# Revit family: Electronics_Visual-Projectors_ViewSonic_The-ViewSonicR-PRO8510L-Projector
name_source: partatom
category: Electrical Equipment
revit_build: Autodesk Revit 2015 (Build: 20140606_1530(x64)
units: mm (PartAtom-declared; Revit-internal decimal feet)

## types (1)
- PRO8510L
    Assembly Code = D50
    BIMobject category = Visual - Projectors
    BIMobject category code = electronics-visual-projectors
    BIMobject main category = Electronics
    BIMobject main category code = electronics
    BOSUseNativeGeometries = 1
    Brand url = https://www.viewsonic.com
    Covering Color = Plastic - Viewsonic - White
    Description = Delivering 1024 x 768 resolution and 5200 lumens of brightness, the ViewSonic® LightStream® Pro8510L is the ideal XGA projector for professional installations, large venues, and business and education environments. With its 1.6x optical zoom, centered lens, vertical lens shift, and HV keystoning, the Pro8510L provides extreme flexibility even in the most challenging installations. The Pro8510L boasts a sleek top cover design for quick lamp and accessory access, while an intuitive PortAll® compartment accommodates additional accessories such as an HDBT receiver, wireless streaming device, or PC stick. The cable management hood hides unsightly cables, and a 4-in-1 power button serves as a central point for LED notifications. Moreover, four HDMI ports and additional audio and video ports allow for extensive connectivity to handle multiple devices without the need to switch cables. Powered by SuperColor™ technology for beautiful image reproduction, and SonicExpert™ technology for incredibly clear sound, the Pro8510L delivers a professional audiovisual performance.
    Design country = Taiwan
    Edition number = 1
    Keynote = V90
    Manufacturer = ViewSonic
    Manufacturer country = Taiwan
    Manufacturer name = ViewSonic
    Model = viewsonic_8510L
    Product Guid = a43baa1d-4d28-4565-8a64-71fbe028e622
    Product SKU = viewsonic_PRO8530HDL
    Product data url = https://bimobject.com
    Product family = Electronics
    Product group = Projectors
    Product name = The ViewSonic® PRO8530HDL Projector
    Product url = https://www.viewsonic.com
    QR code = http://bimobject.com
    URL = www.viewsonic.com
    a = Image Aspect Ratio : "4  - 3"
    b = Image Aspect Ratio : "16 - 9"
    c = Image Aspect Ratio : "16 - 10"

## geometry (parser evidence)
native form markers: Blend x2, Sweep x7
no freeform markers — native parametric forms only
